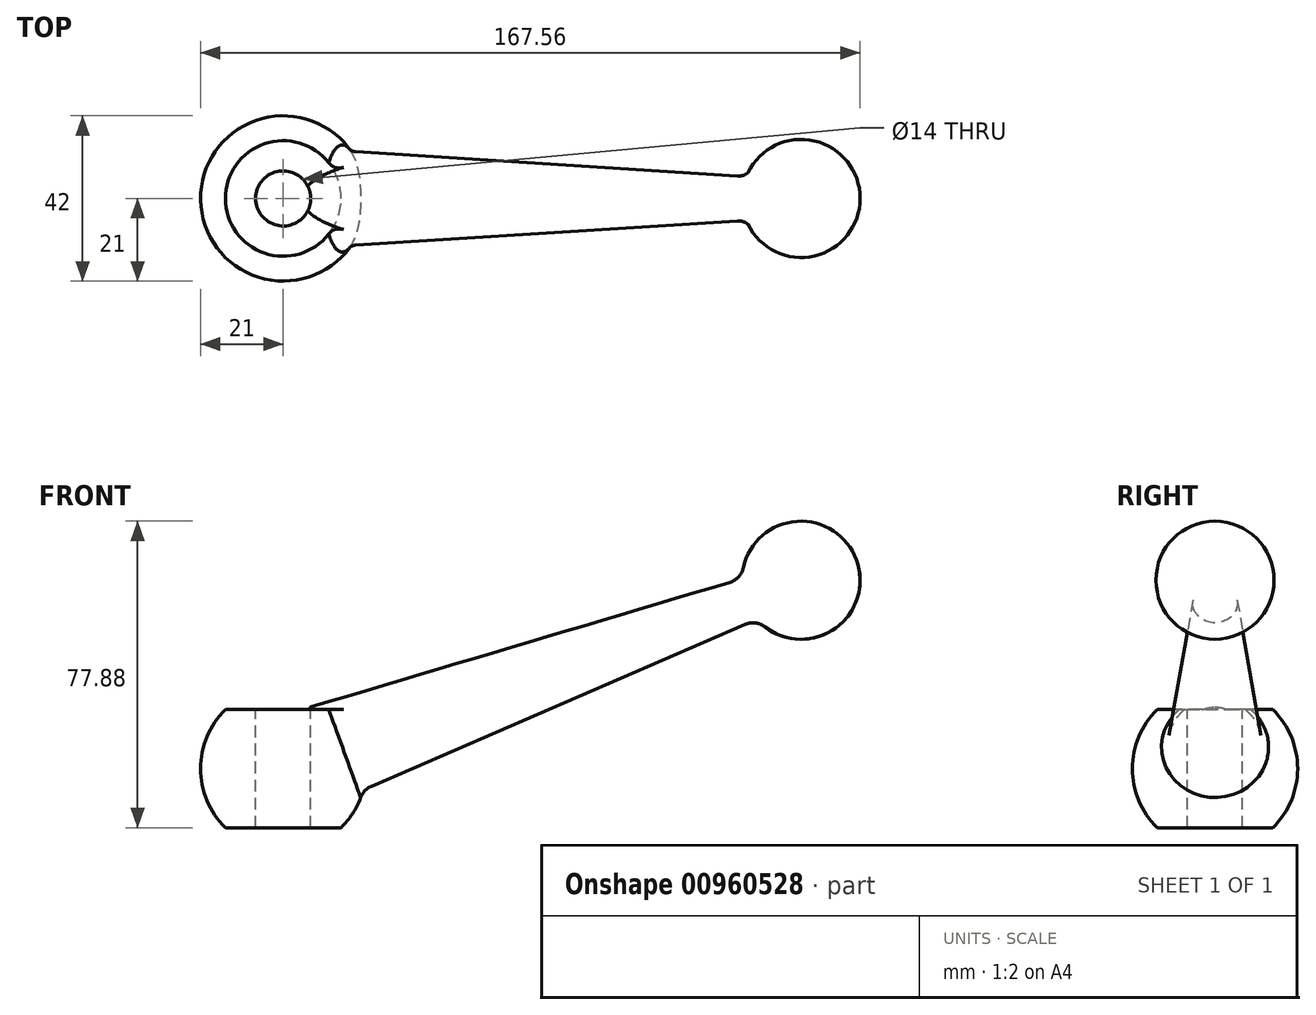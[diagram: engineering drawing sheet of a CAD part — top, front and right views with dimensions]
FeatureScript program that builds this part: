
annotation { "Feature Type Name" : "Feature", "Feature Type Description" : "" }
export const myFeature = defineFeature(function(context is Context, id is Id, definition is map)
    precondition{}
    {
        {
            var Q0;
            Q0=qCreatedBy(makeId("Front.planeOp"),FACE);
            var sketch = newSketch(context, id + "F0", { "sketchPlane" : qUnion([Q0])});
            skArc(sketch, "E0", {"start": v(12.1, 17.17) * mm, "mid": v(-16.68, -12.76) * mm, "end": v(19.73, 7.18) * mm});
            skLineSegment(sketch, "E1", {"start": v(-14.7, 15) * mm, "end": v(4.8, 15) * mm});
            skLineSegment(sketch, "E2", {"start": v(-14.7, -15) * mm, "end": v(42.62, -15) * mm});
            skLineSegment(sketch, "E3", {"start": v(0, 21) * mm, "end": v(0, -21) * mm});
            skCircle(sketch, "E4", {"center": v(131.56, 47.88) * mm, "radius": 15 * mm});
            skLineSegment(sketch, "E5", {"start": v(0, 0) * mm, "end": v(145.65, 53.01) * mm});
            skLineSegment(sketch, "E6", {"start": v(116.56, 48.28) * mm, "end": v(0, 13.57) * mm});
            skLineSegment(sketch, "E7", {"start": v(120.32, 37.94) * mm, "end": v(0, -14.17) * mm});
            skPoint(sketch, "E8.orphan", {"position": v(12.1, 17.17) * mm});
            skPoint(sketch, "E9.orphan", {"position": v(20.3, -5.38) * mm});
            skSolve(sketch);
        }
        {
            var Q0;
            {var subQ1=sQuery(id+"F0.wireOp",EDGE,"E0");var subQ6=sQuery(id+"F0.wireOp",EDGE,"E1");var subQ8=makeQuery(id+"F0.imprint","INTERSECT",VERTEX,{"derivedFrom":[subQ1,subQ6]});Q0=makeQuery(id+"F0.imprint","IMPRINT",FACE,{"disambiguationData":[TD([[makeQuery(id+"F0.imprint","IMPRINT",EDGE,{"disambiguationData":[TD([[subQ8,-1.0]])],"derivedFrom":subQ1}),1.0]])]});}
            var Q1;
            Q1=sQuery(id+"F0.wireOp",EDGE,"E3");
            revolve(context, id + "F1", {"surfaceOperationType" : NewSurfaceOperationType.NEW, "entities" : qUnion([Q0]), "axis" : qUnion([Q1]), "revolveType" : RevolveType.FULL});
        }
        {
            var Q0;
            {var subQ0=sQuery(id+"F0.wireOp",EDGE,"E5");var subQ5=sQuery(id+"F0.wireOp",EDGE,"E3");var subQ6=makeQuery(id+"F0.imprint","INTERSECT",VERTEX,{"derivedFrom":[subQ5,subQ0]});Q0=makeQuery(id+"F0.imprint","IMPRINT",FACE,{"disambiguationData":[TD([[makeQuery(id+"F0.imprint","IMPRINT",EDGE,{"disambiguationData":[TD([[subQ6,1.0]])],"derivedFrom":subQ5}),1.0]])]});}
            var Q1;
            {var subQ0=sQuery(id+"F0.wireOp",EDGE,"E5");var subQ1=sQuery(id+"F0.wireOp",EDGE,"E4");var subQ2=makeQuery(id+"F0.imprint","INTERSECT",VERTEX,{"disambiguationData":[OD(0.0)],"derivedFrom":[subQ1,subQ0]});Q1=makeQuery(id+"F0.imprint","IMPRINT",FACE,{"disambiguationData":[TD([[makeQuery(id+"F0.imprint","IMPRINT",EDGE,{"disambiguationData":[TD([[subQ2,-1.0]])],"derivedFrom":subQ1}),1.0]])]});}
            var Q2;
            Q2=sQuery(id+"F0.wireOp",EDGE,"E5");
            revolve(context, id + "F2", {"operationType" : NewBodyOperationType.ADD, "surfaceOperationType" : NewSurfaceOperationType.NEW, "entities" : qUnion([Q0, Q1]), "axis" : qUnion([Q2]), "revolveType" : RevolveType.FULL});
        }
        {
            var Q0;
            Q0=makeQuery(id+"F2.boolean.opBoolean","INTERSECT",EDGE,{"derivedFrom":[makeQuery(id+"F1.opRevolve","SWEPT_FACE",FACE,{"disambiguationData":[OSD([sQuery(id+"F0.wireOp",EDGE,"E0")])]}),makeQuery(id+"F2.opRevolve","SWEPT_FACE",FACE,{"disambiguationData":[OSD([sQuery(id+"F0.wireOp",EDGE,"E6")])]})]});
            var Q1;
            Q1=makeQuery(id+"F2.opRevolve","SWEPT_EDGE",EDGE,{"disambiguationData":[OSD([sQuery(id+"F0.wireOp",EDGE,"E4"),sQuery(id+"F0.wireOp",EDGE,"E6")])]});
            fillet(context, id + "F3", {"entities" : qUnion([Q0, Q1]), "radius" : 5 * mm, "tangentPropagation" : true, "allowEdgeOverflow" : false});
        }
        {
            var Q0;
            Q0=makeQuery(id+"F1.opRevolve","SWEPT_FACE",FACE,{"disambiguationData":[OSD([sQuery(id+"F0.wireOp",EDGE,"E2")])]});
            var sketch = newSketch(context, id + "F4", { "sketchPlane" : qUnion([Q0])});
            skPoint(sketch, "E10.0", {"position": v(0, 0) * mm});
            skSolve(sketch);
        }
        {
            var Q0;
            Q0=sQuery(id+"F4.wireOp",VERTEX,"E10.0");
            var Q1;
            Q1=makeQuery(id+"F1.opRevolve","SWEPT_BODY",BODY,{"disambiguationData":[OSD([sQuery(id+"F0.wireOp",EDGE,"E0"),sQuery(id+"F0.wireOp",EDGE,"E1"),sQuery(id+"F0.wireOp",EDGE,"E2"),sQuery(id+"F0.wireOp",EDGE,"E3")])]});
            hole(context, id + "F5", {"style" : HoleStyle.SIMPLE, "endStyle" : HoleEndStyle.THROUGH, "standardTappedOrClearance" : lookupTablePath({ "standard" : "ISO", "engagement" : "75%", "pitch" : "2 mm", "size" : "M16", "type" : "Tapped" }), "standardBlindInLast" : lookupTablePath({ "standard" : "ISO", "fit" : "Normal", "engagement" : "75%", "pitch" : "2 mm", "size" : "M16", "type" : "Clearance & tapped" }), "holeDiameter" : 14 * mm, "majorDiameter" : 16 * mm, "showTappedDepth" : true, "isTappedThrough" : true, "tappedDepth" : 2.75 * mm, "tapClearance" : 3, "startFromSketch" : true, "locations" : qUnion([Q0]), "scope" : qUnion([Q1])});
        }
    });
